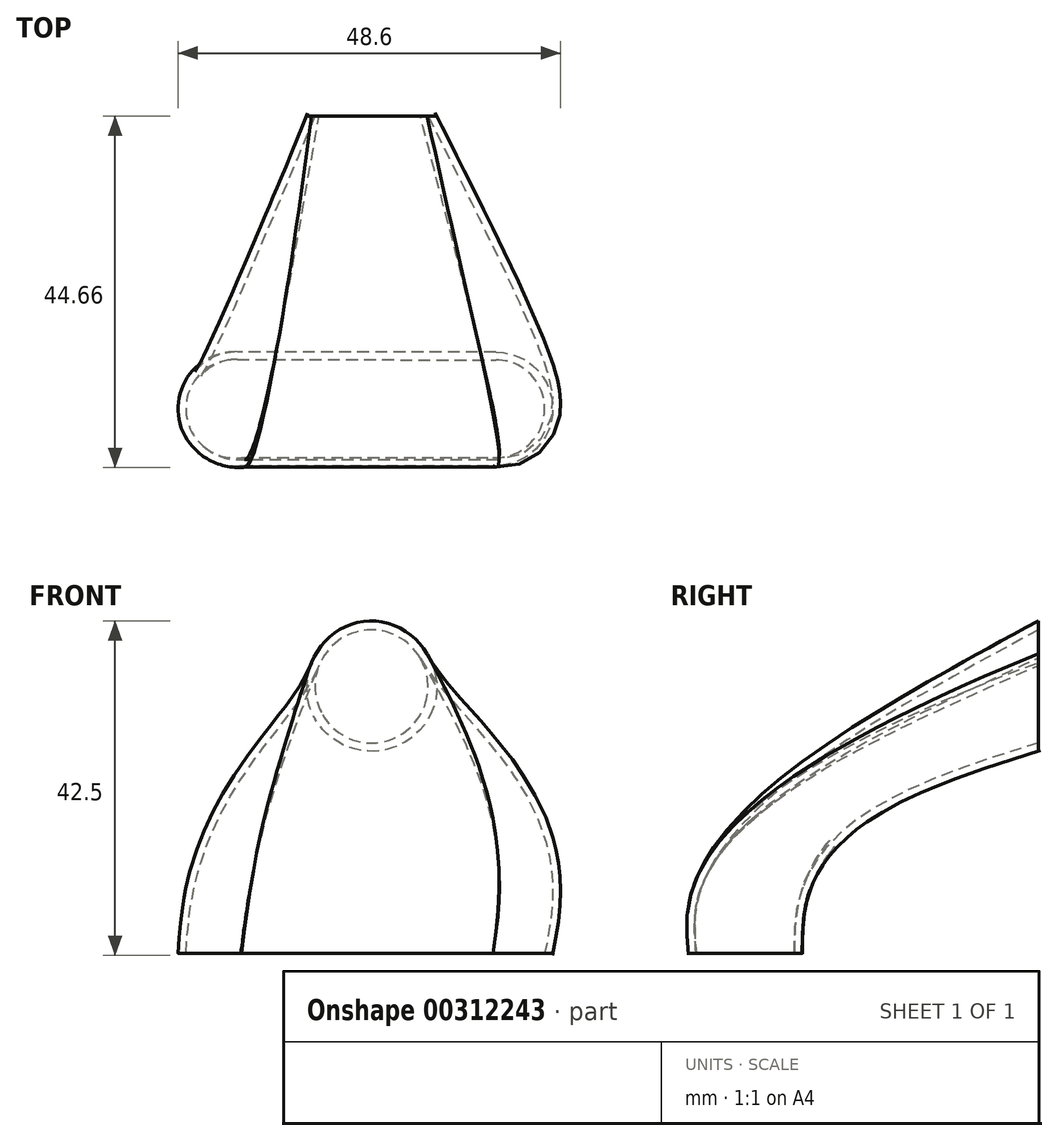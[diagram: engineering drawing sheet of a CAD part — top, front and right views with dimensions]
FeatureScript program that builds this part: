
annotation { "Feature Type Name" : "Feature", "Feature Type Description" : "" }
export const myFeature = defineFeature(function(context is Context, id is Id, definition is map)
    precondition{}
    {
        {
            var Q0;
            Q0=qCreatedBy(makeId("Top.planeOp"),FACE);
            cPlane(context, id + "F0", {"entities" : qUnion([Q0]), "cplaneType" : CPlaneType.OFFSET, "offset" : 5 * mm, "width" : 150 * mm, "height" : 150 * mm});
        }
        {
            var Q0;
            Q0=qCreatedBy(makeId("Front.planeOp"),FACE);
            cPlane(context, id + "F1", {"entities" : qUnion([Q0]), "cplaneType" : CPlaneType.OFFSET, "offset" : 37.2 * mm, "oppositeDirection" : true, "width" : 150 * mm, "height" : 150 * mm});
        }
        {
            var Q0;
            Q0=qCreatedBy(makeId("Top.planeOp"),FACE);
            var sketch = newSketch(context, id + "F2", { "sketchPlane" : qUnion([Q0])});
            skLineSegment(sketch, "E0.0", {"start": v(-16.59, -6.2) * mm, "end": v(15.42, -6.2) * mm});
            skArc(sketch, "E0.1", {"start": v(-17.03, 6.24) * mm, "mid": v(-23.57, -0.22) * mm, "end": v(-16.59, -6.2) * mm});
            skLineSegment(sketch, "E0.2", {"start": v(-17.03, 6.24) * mm, "end": v(15.8, 6.21) * mm});
            skArc(sketch, "E0.3", {"start": v(15.42, -6.2) * mm, "mid": v(22, -0.19) * mm, "end": v(15.8, 6.21) * mm});
            skSolve(sketch);
        }
        {
            var Q0;
            Q0=qCreatedBy(id+"F0.planeOp",FACE);
            var sketch = newSketch(context, id + "F3", { "sketchPlane" : qUnion([Q0])});
            skArc(sketch, "E1.0", {"start": v(-16.36, 6.5) * mm, "mid": v(-23.1, -0.18) * mm, "end": v(-15.9, -6.35) * mm});
            skLineSegment(sketch, "E1.1", {"start": v(-16.36, 6.5) * mm, "end": v(16.46, 6.46) * mm});
            skArc(sketch, "E1.2", {"start": v(16.08, -6.35) * mm, "mid": v(22.86, -0.14) * mm, "end": v(16.46, 6.46) * mm});
            skLineSegment(sketch, "E1.3", {"start": v(-15.9, -6.35) * mm, "end": v(16.08, -6.35) * mm});
            skSolve(sketch);
        }
        {
            var Q0;
            Q0=qCreatedBy(id+"F1.planeOp",FACE);
            var sketch = newSketch(context, id + "F4", { "sketchPlane" : qUnion([Q0])});
            skArc(sketch, "E2", {"start": v(-6.67, 36.56) * mm, "mid": v(-7.16, 33.4) * mm, "end": v(-6.24, 30.35) * mm});
            skArc(sketch, "E3", {"start": v(-6.24, 30.35) * mm, "mid": v(0.64, 26.75) * mm, "end": v(6.77, 31.51) * mm});
            skArc(sketch, "E4", {"start": v(6.2, 37.53) * mm, "mid": v(-0.54, 41.06) * mm, "end": v(-6.67, 36.56) * mm});
            skArc(sketch, "E5", {"start": v(6.77, 31.51) * mm, "mid": v(7.15, 34.58) * mm, "end": v(6.2, 37.53) * mm});
            skSolve(sketch);
        }
        {
            var Q0;
            Q0=makeQuery(id+"F2.imprint","IMPRINT",FACE,{"disambiguationData":[TD([[makeQuery(id+"F2.imprint","IMPRINT",EDGE,{"derivedFrom":sQuery(id+"F2.wireOp",EDGE,"E0.0")}),1.0]])]});
            var Q1;
            Q1=makeQuery(id+"F3.imprint","IMPRINT",FACE,{"disambiguationData":[TD([[makeQuery(id+"F3.imprint","IMPRINT",EDGE,{"derivedFrom":sQuery(id+"F3.wireOp",EDGE,"E1.0")}),1.0]])]});
            var Q2;
            Q2=makeQuery(id+"F4.imprint","IMPRINT",FACE,{"disambiguationData":[TD([[makeQuery(id+"F4.imprint","IMPRINT",EDGE,{"derivedFrom":sQuery(id+"F4.wireOp",EDGE,"E2")}),1.0]])]});
            loft(context, id + "F5", {"sheetProfilesArray" : [{ "sheetProfileEntities" : qUnion([Q0]) }, { "sheetProfileEntities" : qUnion([Q1]) }, { "sheetProfileEntities" : qUnion([Q2]) }]});
        }
        {
            var Q0;
            Q0=makeQuery(id+"F5.opLoft","CAP_FACE",FACE,{"disambiguationData":[OSD([makeQuery(id+"F2.imprint","IMPRINT",FACE,{"disambiguationData":[TD([[makeQuery(id+"F2.imprint","IMPRINT",EDGE,{"derivedFrom":sQuery(id+"F2.wireOp",EDGE,"E0.0")}),1.0]])]})])],"isStart":true});
            var Q1;
            Q1=makeQuery(id+"F5.opLoft","CAP_FACE",FACE,{"disambiguationData":[OSD([makeQuery(id+"F4.imprint","IMPRINT",FACE,{"disambiguationData":[TD([[makeQuery(id+"F4.imprint","IMPRINT",EDGE,{"derivedFrom":sQuery(id+"F4.wireOp",EDGE,"E2")}),1.0]])]})])],"isStart":true});
            shell(context, id + "F6", {"entities" : qUnion([Q0, Q1]), "thickness" : 1 * mm, "oppositeDirection" : true});
        }
    });
